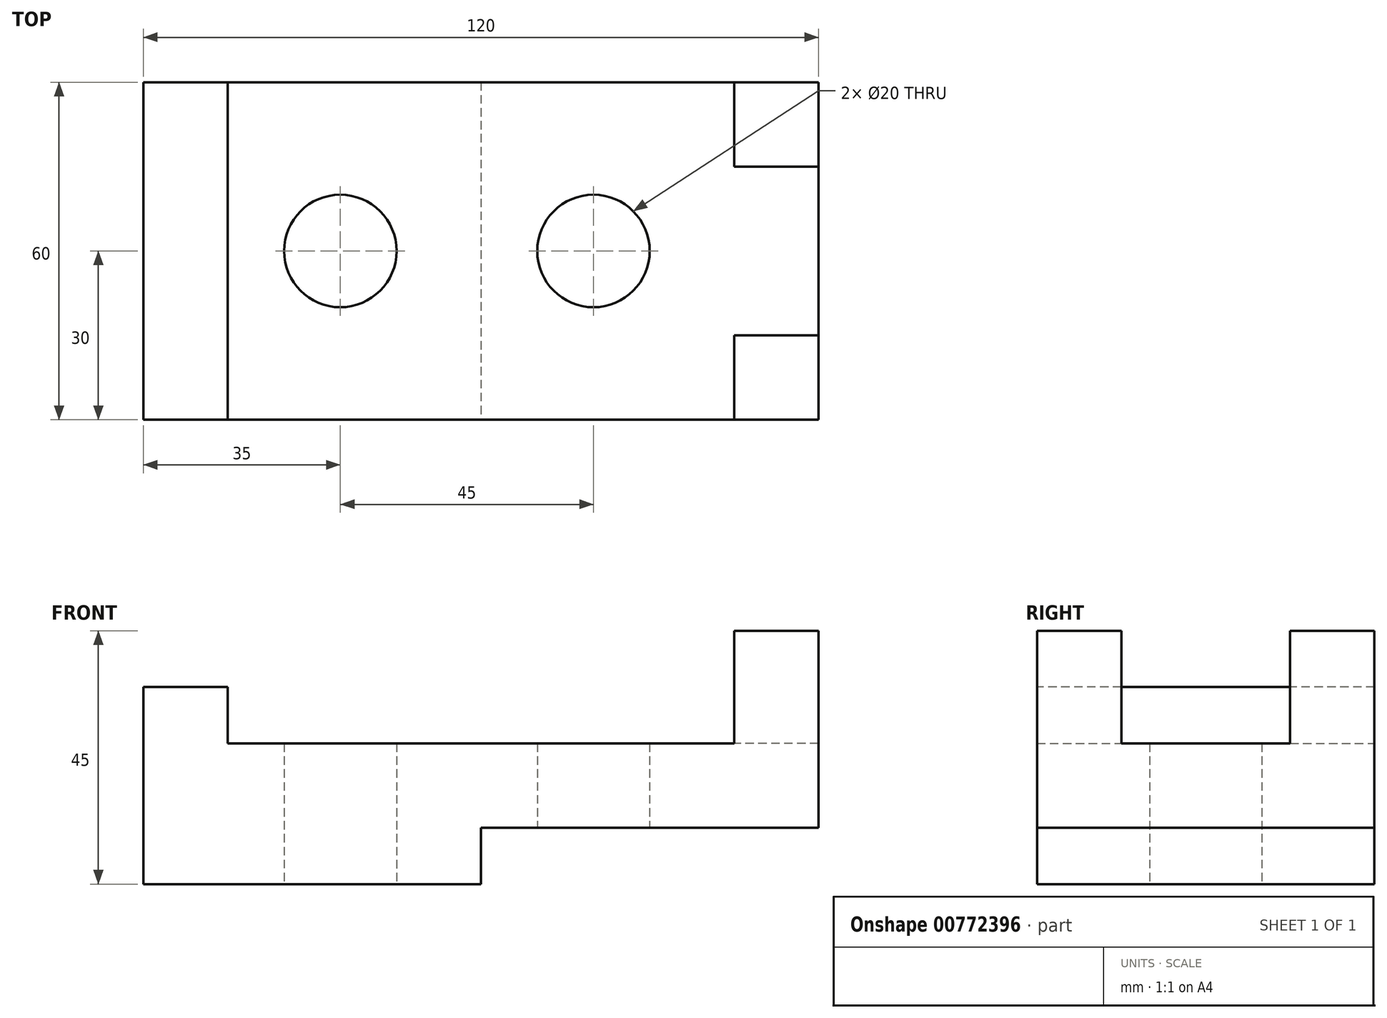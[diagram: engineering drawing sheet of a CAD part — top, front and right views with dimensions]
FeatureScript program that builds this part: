
annotation { "Feature Type Name" : "Feature", "Feature Type Description" : "" }
export const myFeature = defineFeature(function(context is Context, id is Id, definition is map)
    precondition{}
    {
        {
            var Q0;
            Q0=qCreatedBy(makeId("Top.planeOp"),FACE);
            var sketch = newSketch(context, id + "F0", { "sketchPlane" : qUnion([Q0])});
            skLineSegment(sketch, "E0.bottom", {"start": v(-60, 30) * mm, "end": v(60, 30) * mm});
            skLineSegment(sketch, "E0.top", {"start": v(-60, -30) * mm, "end": v(60, -30) * mm});
            skLineSegment(sketch, "E0.left", {"start": v(-60, 30) * mm, "end": v(-60, -30) * mm});
            skLineSegment(sketch, "E0.right", {"start": v(60, 30) * mm, "end": v(60, -30) * mm});
            skPoint(sketch, "E0.middle", {"position": v(0, 0) * mm});
            skLineSegment(sketch, "E1", {"start": v(-45, 30) * mm, "end": v(-45, -30) * mm});
            skLineSegment(sketch, "E2", {"start": v(45, 30) * mm, "end": v(45, 15) * mm});
            skLineSegment(sketch, "E3", {"start": v(45, -30) * mm, "end": v(45, -30) * mm});
            skLineSegment(sketch, "E4", {"start": v(0, 30) * mm, "end": v(0, -30) * mm});
            skLineSegment(sketch, "E5", {"start": v(45, 15) * mm, "end": v(60, 15) * mm});
            skLineSegment(sketch, "E6", {"start": v(45, -15) * mm, "end": v(60, -15) * mm});
            skLineSegment(sketch, "E7.trimOffspring", {"start": v(45, -15) * mm, "end": v(45, -30) * mm});
            skLineSegment(sketch, "E8", {"start": v(-60, 0) * mm, "end": v(60, 0) * mm, "construction": true});
            skCircle(sketch, "E9", {"center": v(-25, 0) * mm, "radius": 10 * mm});
            skCircle(sketch, "E10", {"center": v(20, 0) * mm, "radius": 10 * mm});
            skSolve(sketch);
        }
        {
            var Q0;
            Q0=qSketchRegion(id+"F0",true);
            extrude(context, id + "F1", {"entities" : qUnion([Q0]), "depth" : 25 * mm, "offsetDistance" : 25 * mm});
        }
        {
            var Q0;
            {var subQ4=sQuery(id+"F0.wireOp",EDGE,"E6");Q0=makeQuery(id+"F0.imprint","IMPRINT",FACE,{"disambiguationData":[TD([[makeQuery(id+"F0.imprint","IMPRINT",EDGE,{"derivedFrom":subQ4}),-1.0]])]});}
            var Q1;
            {var subQ3=sQuery(id+"F0.wireOp",EDGE,"E2");Q1=makeQuery(id+"F0.imprint","IMPRINT",FACE,{"disambiguationData":[TD([[makeQuery(id+"F0.imprint","IMPRINT",EDGE,{"derivedFrom":subQ3}),1.0]])]});}
            extrude(context, id + "F2", {"entities" : qUnion([Q0, Q1]), "operationType" : NewBodyOperationType.ADD, "depth" : 45 * mm, "offsetDistance" : 25 * mm});
        }
        {
            var Q0;
            {var subQ0=sQuery(id+"F0.wireOp",EDGE,"E0.left");Q0=makeQuery(id+"F0.imprint","IMPRINT",FACE,{"disambiguationData":[TD([[makeQuery(id+"F0.imprint","IMPRINT",EDGE,{"derivedFrom":subQ0}),1.0]])]});}
            extrude(context, id + "F3", {"entities" : qUnion([Q0]), "operationType" : NewBodyOperationType.ADD, "depth" : 35 * mm, "offsetDistance" : 25 * mm});
        }
        {
            var Q0;
            {var subQ0=sQuery(id+"F0.wireOp",EDGE,"E2");Q0=makeQuery(id+"F0.imprint","IMPRINT",FACE,{"disambiguationData":[TD([[makeQuery(id+"F0.imprint","IMPRINT",EDGE,{"derivedFrom":subQ0}),-1.0]])]});}
            var Q1;
            {var subQ4=sQuery(id+"F0.wireOp",EDGE,"E6");Q1=makeQuery(id+"F0.imprint","IMPRINT",FACE,{"disambiguationData":[TD([[makeQuery(id+"F0.imprint","IMPRINT",EDGE,{"derivedFrom":subQ4}),-1.0]])]});}
            var Q2;
            {var subQ3=sQuery(id+"F0.wireOp",EDGE,"E2");Q2=makeQuery(id+"F0.imprint","IMPRINT",FACE,{"disambiguationData":[TD([[makeQuery(id+"F0.imprint","IMPRINT",EDGE,{"derivedFrom":subQ3}),1.0]])]});}
            extrude(context, id + "F4", {"entities" : qUnion([Q0, Q1, Q2]), "operationType" : NewBodyOperationType.REMOVE, "depth" : 10 * mm, "offsetDistance" : 25 * mm});
        }
    });
